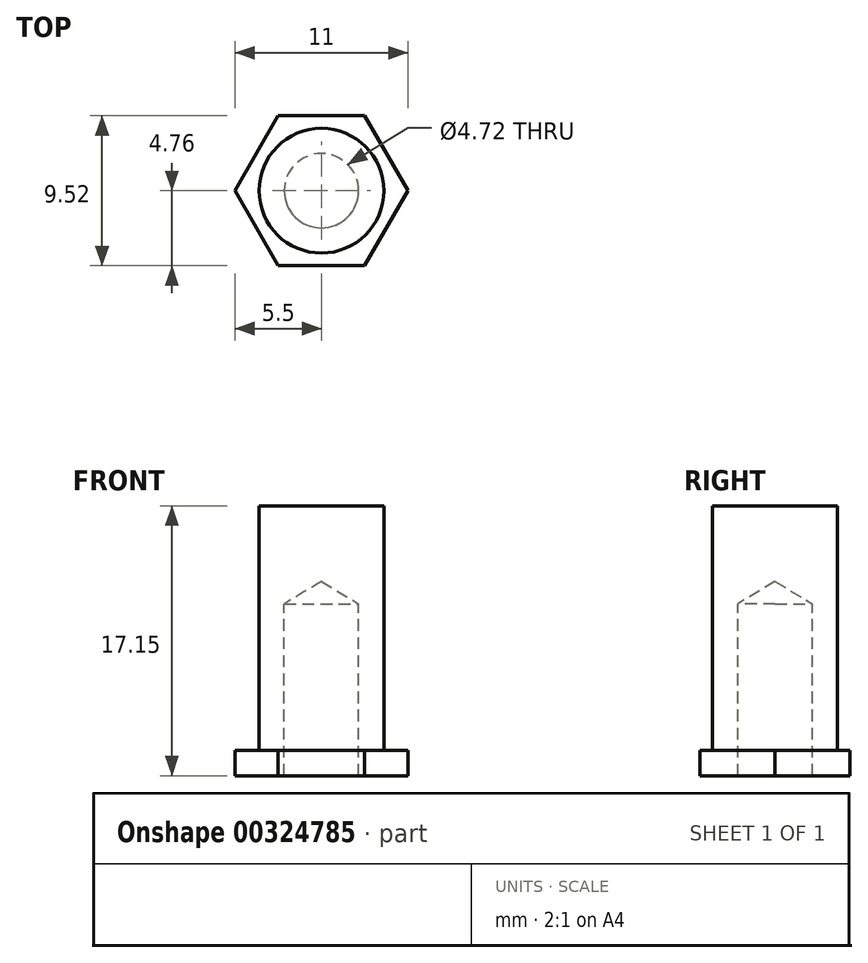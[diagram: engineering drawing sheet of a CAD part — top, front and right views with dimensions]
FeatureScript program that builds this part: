
annotation { "Feature Type Name" : "Feature", "Feature Type Description" : "" }
export const myFeature = defineFeature(function(context is Context, id is Id, definition is map)
    precondition{}
    {
        {
            var Q0;
            Q0=qCreatedBy(makeId("Top.planeOp"),FACE);
            var sketch = newSketch(context, id + "F0", { "sketchPlane" : qUnion([Q0])});
            skCircle(sketch, "E0", {"center": v(0, 0) * mm, "radius": 5.5 * mm, "construction": true});
            skLineSegment(sketch, "E1", {"start": v(-2.38, 17.09) * mm, "end": v(-2.38, -23.89) * mm, "construction": true});
            skLineSegment(sketch, "E2.MirrorCS", {"start": v(2.38, 17.09) * mm, "end": v(2.38, -23.89) * mm, "construction": true});
            skLineSegment(sketch, "E3", {"start": v(0, 0) * mm, "end": v(6.4, 11.08) * mm});
            skLineSegment(sketch, "E4", {"start": v(2.75, 4.76) * mm, "end": v(-2.75, 4.76) * mm});
            skLineSegment(sketch, "E5", {"start": v(-2.75, 4.76) * mm, "end": v(-5.5, 0) * mm});
            skLineSegment(sketch, "E6", {"start": v(2.75, 4.76) * mm, "end": v(5.5, 0) * mm});
            skLineSegment(sketch, "E7.MirrorCS", {"start": v(-2.75, -4.76) * mm, "end": v(-5.5, 0) * mm});
            skLineSegment(sketch, "E8.MirrorCS", {"start": v(2.75, -4.76) * mm, "end": v(-2.75, -4.76) * mm});
            skLineSegment(sketch, "E9.MirrorCS", {"start": v(2.75, -4.76) * mm, "end": v(5.5, 0) * mm});
            skSolve(sketch);
        }
        {
            var Q0;
            Q0=makeQuery(id+"F0.imprint","IMPRINT",FACE,{"disambiguationData":[TD([[makeQuery(id+"F0.imprint","IMPRINT",EDGE,{"derivedFrom":sQuery(id+"F0.wireOp",EDGE,"IJnFrozW-OVpm-AC47-Letx-wI6fYjEJorTy")}),-1.0]])]});
            var Q1;
            Q1=makeQuery(id+"F0.imprint","IMPRINT",FACE,{"disambiguationData":[TD([[makeQuery(id+"F0.imprint","IMPRINT",EDGE,{"derivedFrom":sQuery(id+"F0.wireOp",EDGE,"E4")}),1.0]])]});
            extrude(context, id + "F1", {"entities" : qUnion([Q0, Q1]), "depth" : 1.6 * mm, "offsetDistance" : 25.4 * mm});
        }
        {
            var Q0;
            Q0=makeQuery(id+"F1.opExtrude","CAP_FACE",FACE,{"disambiguationData":[OSD([sQuery(id+"F0.wireOp",EDGE,"E4"),sQuery(id+"F0.wireOp",EDGE,"E5"),sQuery(id+"F0.wireOp",EDGE,"E6"),sQuery(id+"F0.wireOp",EDGE,"E7.MirrorCS"),sQuery(id+"F0.wireOp",EDGE,"E8.MirrorCS"),sQuery(id+"F0.wireOp",EDGE,"E9.MirrorCS")])],"isStart":false});
            var sketch = newSketch(context, id + "F2", { "sketchPlane" : qUnion([Q0])});
            skCircle(sketch, "E10", {"center": v(0, 0) * mm, "radius": 3.96 * mm});
            skSolve(sketch);
        }
        {
            var Q0;
            Q0=makeQuery(id+"F2.imprint","IMPRINT",FACE,{"disambiguationData":[TD([[makeQuery(id+"F2.imprint","IMPRINT",EDGE,{"derivedFrom":sQuery(id+"F2.wireOp",EDGE,"E10")}),1.0]])]});
            extrude(context, id + "F3", {"entities" : qUnion([Q0]), "operationType" : NewBodyOperationType.ADD, "depth" : 15.54 * mm, "offsetDistance" : 25.4 * mm});
        }
        {
            var Q0;
            Q0=makeQuery(id+"F1.opExtrude","CAP_FACE",FACE,{"disambiguationData":[OSD([sQuery(id+"F0.wireOp",EDGE,"E4"),sQuery(id+"F0.wireOp",EDGE,"E5"),sQuery(id+"F0.wireOp",EDGE,"E6"),sQuery(id+"F0.wireOp",EDGE,"E7.MirrorCS"),sQuery(id+"F0.wireOp",EDGE,"E8.MirrorCS"),sQuery(id+"F0.wireOp",EDGE,"E9.MirrorCS")])],"isStart":true});
            var sketch = newSketch(context, id + "F4", { "sketchPlane" : qUnion([Q0])});
            skPoint(sketch, "E11", {"position": v(0, 0) * mm});
            skSolve(sketch);
        }
        {
            var Q0;
            Q0=sQuery(id+"F4.wireOp",VERTEX,"E11");
            var Q1;
            Q1=makeQuery(id+"F1.opExtrude","SWEPT_BODY",BODY,{"disambiguationData":[OSD([sQuery(id+"F0.wireOp",EDGE,"E4"),sQuery(id+"F0.wireOp",EDGE,"E5"),sQuery(id+"F0.wireOp",EDGE,"E6"),sQuery(id+"F0.wireOp",EDGE,"E7.MirrorCS"),sQuery(id+"F0.wireOp",EDGE,"E8.MirrorCS"),sQuery(id+"F0.wireOp",EDGE,"E9.MirrorCS")])]});
            hole(context, id + "F5", {"style" : HoleStyle.SIMPLE, "endStyle" : HoleEndStyle.BLIND, "holeDiameter" : 4.72 * mm, "majorDiameter" : 6.35 * mm, "holeDepth" : 10.92 * mm, "tappedDepth" : 12.7 * mm, "tapClearance" : 3, "locations" : qUnion([Q0]), "scope" : qUnion([Q1])});
        }
    });
